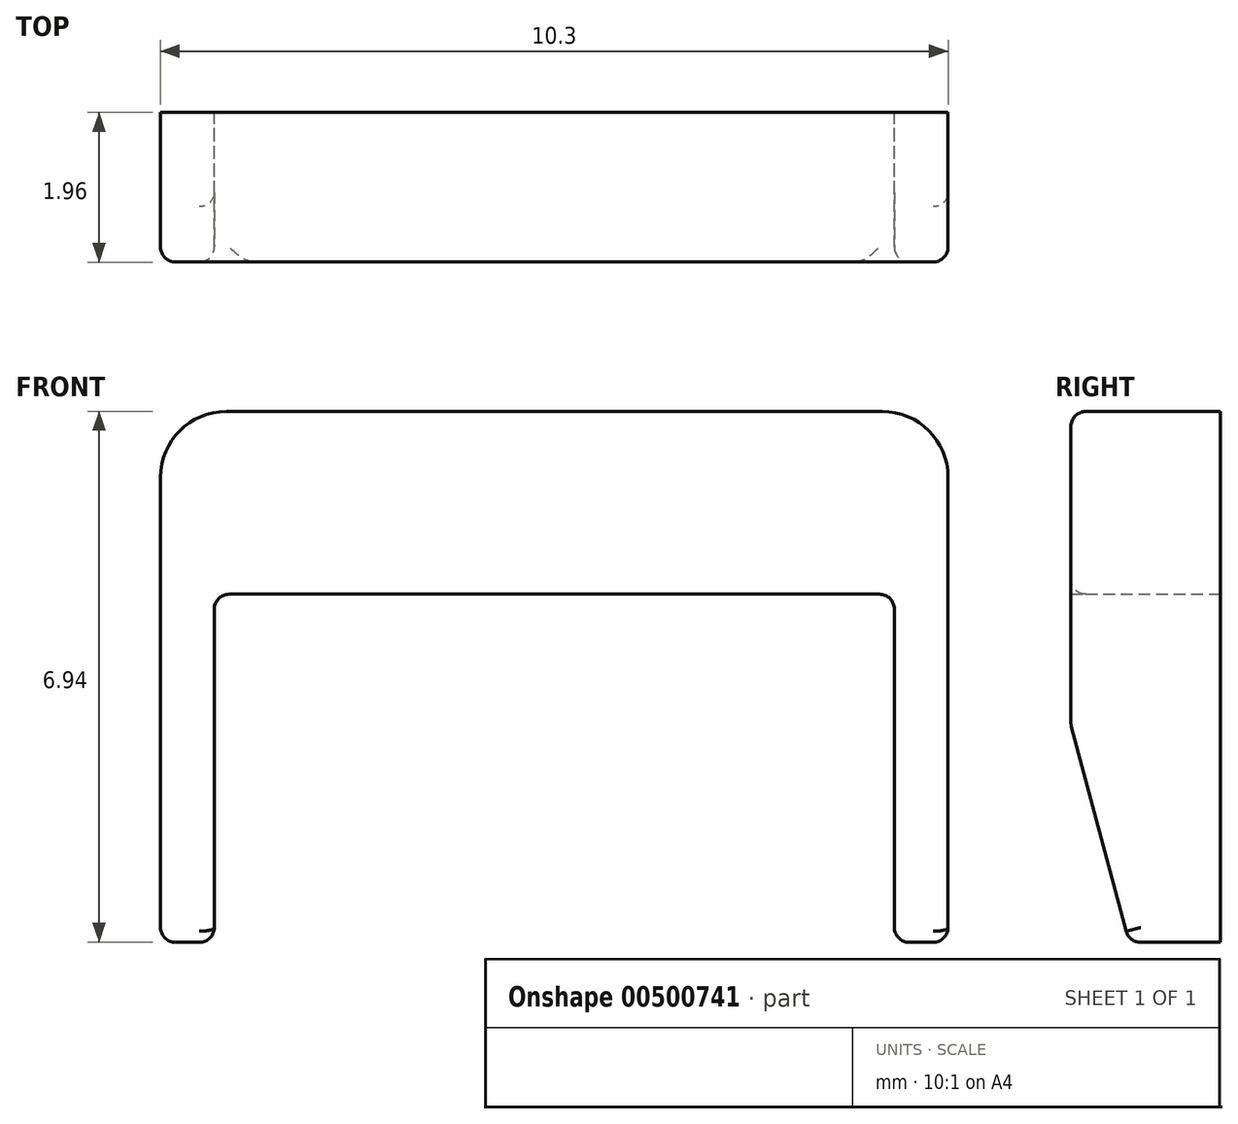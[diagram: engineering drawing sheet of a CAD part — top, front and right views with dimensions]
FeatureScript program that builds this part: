
annotation { "Feature Type Name" : "Feature", "Feature Type Description" : "" }
export const myFeature = defineFeature(function(context is Context, id is Id, definition is map)
    precondition{}
    {
        {
            var Q0;
            Q0=qCreatedBy(makeId("Front.planeOp"),FACE);
            var sketch = newSketch(context, id + "F0", { "sketchPlane" : qUnion([Q0])});
            skLineSegment(sketch, "E0.bottom", {"start": v(-48.29, 36.5) * mm, "end": v(-38, 36.5) * mm});
            skLineSegment(sketch, "E0.top", {"start": v(-47.58, 34.1) * mm, "end": v(-38.7, 34.1) * mm});
            skLineSegment(sketch, "E0.left", {"start": v(-48.29, 36.5) * mm, "end": v(-48.29, 34.1) * mm});
            skLineSegment(sketch, "E0.right", {"start": v(-38, 36.5) * mm, "end": v(-38, 34.1) * mm});
            skLineSegment(sketch, "E1", {"start": v(-43.14, 34.1) * mm, "end": v(-47.58, 34.1) * mm});
            skLineSegment(sketch, "E2", {"start": v(-43.14, 34.1) * mm, "end": v(-38.7, 34.1) * mm});
            skLineSegment(sketch, "E3", {"start": v(-47.58, 34.1) * mm, "end": v(-47.58, 29.56) * mm});
            skLineSegment(sketch, "E4", {"start": v(-47.58, 29.56) * mm, "end": v(-48.29, 29.56) * mm});
            skLineSegment(sketch, "E5", {"start": v(-48.29, 29.56) * mm, "end": v(-48.29, 34.1) * mm});
            skLineSegment(sketch, "E6", {"start": v(-38.7, 29.56) * mm, "end": v(-38, 29.56) * mm});
            skLineSegment(sketch, "E7", {"start": v(-38.7, 34.1) * mm, "end": v(-38.7, 29.56) * mm});
            skLineSegment(sketch, "E8", {"start": v(-38, 34.1) * mm, "end": v(-38, 29.56) * mm});
            skPoint(sketch, "E9.start.orphan", {"position": v(-43.14, 36.5) * mm});
            skSolve(sketch);
        }
        {
            var Q0;
            Q0=makeQuery(id+"F0.imprint","IMPRINT",FACE,{"disambiguationData":[TD([[makeQuery(id+"F0.imprint","IMPRINT",EDGE,{"derivedFrom":sQuery(id+"F0.wireOp",EDGE,"E0.bottom")}),-1.0]])]});
            extrude(context, id + "F1", {"entities" : qUnion([Q0]), "depth" : 1.96 * mm});
        }
        {
            var Q0;
            Q0=makeQuery(id+"F1.opExtrude","CAP_EDGE",EDGE,{"disambiguationData":[OSD([sQuery(id+"F0.wireOp",EDGE,"E4")])],"isStart":false});
            var Q1;
            Q1=makeQuery(id+"F1.opExtrude","CAP_EDGE",EDGE,{"disambiguationData":[OSD([sQuery(id+"F0.wireOp",EDGE,"E6")])],"isStart":false});
            chamfer(context, id + "F2", {"entities" : qUnion([Q0, Q1]), "chamferType" : ChamferType.OFFSET_ANGLE, "width" : 0.76 * mm, "oppositeDirection" : false, "angle" : 75 * degree, "tangentPropagation" : true});
        }
        {
            var Q0;
            {var subQ0=sQuery(id+"F0.wireOp",EDGE,"E4");Q0=makeQuery(id+"F2.opChamfer","BLEND_EDGE",EDGE,{"blendedFrom":[makeQuery(id+"F1.opExtrude","CAP_EDGE",EDGE,{"disambiguationData":[OSD([subQ0])],"isStart":false}),makeQuery(id+"F1.opExtrude","SWEPT_FACE",FACE,{"disambiguationData":[OSD([subQ0])]})],"blendedInto":[makeQuery(id+"F1.opExtrude","SWEPT_FACE",FACE,{"disambiguationData":[OSD([subQ0])]})]});}
            var Q1;
            {var subQ0=sQuery(id+"F0.wireOp",EDGE,"E6");Q1=makeQuery(id+"F2.opChamfer","BLEND_EDGE",EDGE,{"blendedFrom":[makeQuery(id+"F1.opExtrude","CAP_EDGE",EDGE,{"disambiguationData":[OSD([subQ0])],"isStart":false}),makeQuery(id+"F1.opExtrude","SWEPT_FACE",FACE,{"disambiguationData":[OSD([subQ0])]})],"blendedInto":[makeQuery(id+"F1.opExtrude","SWEPT_FACE",FACE,{"disambiguationData":[OSD([subQ0])]})]});}
            var Q2;
            Q2=makeQuery(id+"F2.opChamfer","BLEND_EDGE",EDGE,{"blendedFrom":[makeQuery(id+"F1.opExtrude","CAP_EDGE",EDGE,{"disambiguationData":[OSD([sQuery(id+"F0.wireOp",EDGE,"E6")])],"isStart":false}),makeQuery(id+"F1.opExtrude","SWEPT_FACE",FACE,{"disambiguationData":[OSD([sQuery(id+"F0.wireOp",EDGE,"E0.right"),sQuery(id+"F0.wireOp",EDGE,"E8")])]})],"blendedInto":[makeQuery(id+"F1.opExtrude","SWEPT_FACE",FACE,{"disambiguationData":[OSD([sQuery(id+"F0.wireOp",EDGE,"E0.right"),sQuery(id+"F0.wireOp",EDGE,"E8")])]})]});
            var Q3;
            Q3=makeQuery(id+"F2.opChamfer","BLEND_EDGE",EDGE,{"blendedFrom":[makeQuery(id+"F1.opExtrude","CAP_EDGE",EDGE,{"disambiguationData":[OSD([sQuery(id+"F0.wireOp",EDGE,"E6")])],"isStart":false}),makeQuery(id+"F1.opExtrude","SWEPT_FACE",FACE,{"disambiguationData":[OSD([sQuery(id+"F0.wireOp",EDGE,"E7")])]})],"blendedInto":[makeQuery(id+"F1.opExtrude","SWEPT_FACE",FACE,{"disambiguationData":[OSD([sQuery(id+"F0.wireOp",EDGE,"E7")])]})]});
            var Q4;
            {var subQ0=sQuery(id+"F0.wireOp",EDGE,"E6");Q4=makeQuery(id+"F2.opChamfer","BLEND_EDGE",EDGE,{"blendedFrom":[makeQuery(id+"F1.opExtrude","CAP_EDGE",EDGE,{"disambiguationData":[OSD([subQ0])],"isStart":false}),makeQuery(id+"F1.opExtrude","CAP_FACE",FACE,{"disambiguationData":[OSD([sQuery(id+"F0.wireOp",EDGE,"E0.bottom"),sQuery(id+"F0.wireOp",EDGE,"E0.left"),sQuery(id+"F0.wireOp",EDGE,"E0.right"),sQuery(id+"F0.wireOp",EDGE,"E1"),sQuery(id+"F0.wireOp",EDGE,"E2"),sQuery(id+"F0.wireOp",EDGE,"E3"),sQuery(id+"F0.wireOp",EDGE,"E4"),sQuery(id+"F0.wireOp",EDGE,"E5"),subQ0,sQuery(id+"F0.wireOp",EDGE,"E7"),sQuery(id+"F0.wireOp",EDGE,"E8")])],"isStart":false})],"blendedInto":[makeQuery(id+"F1.opExtrude","CAP_FACE",FACE,{"disambiguationData":[OSD([sQuery(id+"F0.wireOp",EDGE,"E0.bottom"),sQuery(id+"F0.wireOp",EDGE,"E0.left"),sQuery(id+"F0.wireOp",EDGE,"E0.right"),sQuery(id+"F0.wireOp",EDGE,"E1"),sQuery(id+"F0.wireOp",EDGE,"E2"),sQuery(id+"F0.wireOp",EDGE,"E3"),sQuery(id+"F0.wireOp",EDGE,"E4"),sQuery(id+"F0.wireOp",EDGE,"E5"),subQ0,sQuery(id+"F0.wireOp",EDGE,"E7"),sQuery(id+"F0.wireOp",EDGE,"E8")])],"isStart":false})]});}
            var Q5;
            Q5=makeQuery(id+"F1.opExtrude","CAP_EDGE",EDGE,{"disambiguationData":[OSD([sQuery(id+"F0.wireOp",EDGE,"E1"),sQuery(id+"F0.wireOp",EDGE,"E2")])],"isStart":false});
            var Q6;
            Q6=makeQuery(id+"F2.opChamfer","BLEND_EDGE",EDGE,{"blendedFrom":[makeQuery(id+"F1.opExtrude","CAP_EDGE",EDGE,{"disambiguationData":[OSD([sQuery(id+"F0.wireOp",EDGE,"E4")])],"isStart":false}),makeQuery(id+"F1.opExtrude","SWEPT_FACE",FACE,{"disambiguationData":[OSD([sQuery(id+"F0.wireOp",EDGE,"E3")])]})],"blendedInto":[makeQuery(id+"F1.opExtrude","SWEPT_FACE",FACE,{"disambiguationData":[OSD([sQuery(id+"F0.wireOp",EDGE,"E3")])]})]});
            var Q7;
            Q7=makeQuery(id+"F2.opChamfer","BLEND_EDGE",EDGE,{"blendedFrom":[makeQuery(id+"F1.opExtrude","CAP_EDGE",EDGE,{"disambiguationData":[OSD([sQuery(id+"F0.wireOp",EDGE,"E4")])],"isStart":false}),makeQuery(id+"F1.opExtrude","SWEPT_FACE",FACE,{"disambiguationData":[OSD([sQuery(id+"F0.wireOp",EDGE,"E0.left"),sQuery(id+"F0.wireOp",EDGE,"E5")])]})],"blendedInto":[makeQuery(id+"F1.opExtrude","SWEPT_FACE",FACE,{"disambiguationData":[OSD([sQuery(id+"F0.wireOp",EDGE,"E0.left"),sQuery(id+"F0.wireOp",EDGE,"E5")])]})]});
            var Q8;
            {var subQ0=sQuery(id+"F0.wireOp",EDGE,"E4");Q8=makeQuery(id+"F2.opChamfer","BLEND_EDGE",EDGE,{"blendedFrom":[makeQuery(id+"F1.opExtrude","CAP_EDGE",EDGE,{"disambiguationData":[OSD([subQ0])],"isStart":false}),makeQuery(id+"F1.opExtrude","CAP_FACE",FACE,{"disambiguationData":[OSD([sQuery(id+"F0.wireOp",EDGE,"E0.bottom"),sQuery(id+"F0.wireOp",EDGE,"E0.left"),sQuery(id+"F0.wireOp",EDGE,"E0.right"),sQuery(id+"F0.wireOp",EDGE,"E1"),sQuery(id+"F0.wireOp",EDGE,"E2"),sQuery(id+"F0.wireOp",EDGE,"E3"),subQ0,sQuery(id+"F0.wireOp",EDGE,"E5"),sQuery(id+"F0.wireOp",EDGE,"E6"),sQuery(id+"F0.wireOp",EDGE,"E7"),sQuery(id+"F0.wireOp",EDGE,"E8")])],"isStart":false})],"blendedInto":[makeQuery(id+"F1.opExtrude","CAP_FACE",FACE,{"disambiguationData":[OSD([sQuery(id+"F0.wireOp",EDGE,"E0.bottom"),sQuery(id+"F0.wireOp",EDGE,"E0.left"),sQuery(id+"F0.wireOp",EDGE,"E0.right"),sQuery(id+"F0.wireOp",EDGE,"E1"),sQuery(id+"F0.wireOp",EDGE,"E2"),sQuery(id+"F0.wireOp",EDGE,"E3"),subQ0,sQuery(id+"F0.wireOp",EDGE,"E5"),sQuery(id+"F0.wireOp",EDGE,"E6"),sQuery(id+"F0.wireOp",EDGE,"E7"),sQuery(id+"F0.wireOp",EDGE,"E8")])],"isStart":false})]});}
            var Q9;
            Q9=makeQuery(id+"F1.opExtrude","CAP_EDGE",EDGE,{"disambiguationData":[OSD([sQuery(id+"F0.wireOp",EDGE,"E3")])],"isStart":false});
            var Q10;
            Q10=makeQuery(id+"F1.opExtrude","CAP_EDGE",EDGE,{"disambiguationData":[OSD([sQuery(id+"F0.wireOp",EDGE,"E7")])],"isStart":false});
            var Q11;
            Q11=makeQuery(id+"F1.opExtrude","CAP_EDGE",EDGE,{"disambiguationData":[OSD([sQuery(id+"F0.wireOp",EDGE,"E0.right"),sQuery(id+"F0.wireOp",EDGE,"E8")])],"isStart":false});
            var Q12;
            Q12=makeQuery(id+"F1.opExtrude","SWEPT_EDGE",EDGE,{"disambiguationData":[OSD([sQuery(id+"F0.wireOp",EDGE,"E6"),sQuery(id+"F0.wireOp",EDGE,"E7")])]});
            var Q13;
            Q13=makeQuery(id+"F1.opExtrude","SWEPT_EDGE",EDGE,{"disambiguationData":[OSD([sQuery(id+"F0.wireOp",EDGE,"E6"),sQuery(id+"F0.wireOp",EDGE,"E8")])]});
            var Q14;
            Q14=makeQuery(id+"F1.opExtrude","SWEPT_EDGE",EDGE,{"disambiguationData":[OSD([sQuery(id+"F0.wireOp",EDGE,"E2"),sQuery(id+"F0.wireOp",EDGE,"E7")])]});
            var Q15;
            Q15=makeQuery(id+"F1.opExtrude","SWEPT_EDGE",EDGE,{"disambiguationData":[OSD([sQuery(id+"F0.wireOp",EDGE,"E1"),sQuery(id+"F0.wireOp",EDGE,"E3")])]});
            var Q16;
            Q16=makeQuery(id+"F1.opExtrude","SWEPT_EDGE",EDGE,{"disambiguationData":[OSD([sQuery(id+"F0.wireOp",EDGE,"E3"),sQuery(id+"F0.wireOp",EDGE,"E4")])]});
            var Q17;
            Q17=makeQuery(id+"F1.opExtrude","SWEPT_EDGE",EDGE,{"disambiguationData":[OSD([sQuery(id+"F0.wireOp",EDGE,"E4"),sQuery(id+"F0.wireOp",EDGE,"E5")])]});
            var Q18;
            Q18=makeQuery(id+"F1.opExtrude","CAP_EDGE",EDGE,{"disambiguationData":[OSD([sQuery(id+"F0.wireOp",EDGE,"E0.left"),sQuery(id+"F0.wireOp",EDGE,"E5")])],"isStart":false});
            var Q19;
            Q19=makeQuery(id+"F1.opExtrude","CAP_EDGE",EDGE,{"disambiguationData":[OSD([sQuery(id+"F0.wireOp",EDGE,"E0.bottom")])],"isStart":false});
            fillet(context, id + "F3", {"entities" : qUnion([Q0, Q1, Q2, Q3, Q4, Q5, Q6, Q7, Q8, Q9, Q10, Q11, Q12, Q13, Q14, Q15, Q16, Q17, Q18, Q19]), "radius" : 0.2 * mm, "tangentPropagation" : true, "allowEdgeOverflow" : false});
        }
        {
            var Q0;
            Q0=makeQuery(id+"F1.opExtrude","SWEPT_EDGE",EDGE,{"disambiguationData":[OSD([sQuery(id+"F0.wireOp",EDGE,"E0.bottom"),sQuery(id+"F0.wireOp",EDGE,"E0.right")])]});
            var Q1;
            Q1=makeQuery(id+"F1.opExtrude","SWEPT_EDGE",EDGE,{"disambiguationData":[OSD([sQuery(id+"F0.wireOp",EDGE,"E0.bottom"),sQuery(id+"F0.wireOp",EDGE,"E0.left")])]});
            fillet(context, id + "F4", {"entities" : qUnion([Q0, Q1]), "radius" : 0.86 * mm, "tangentPropagation" : true, "allowEdgeOverflow" : false});
        }
    });
